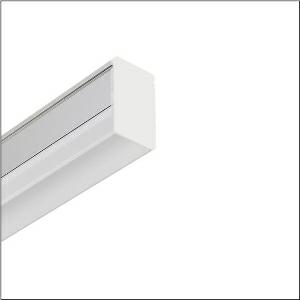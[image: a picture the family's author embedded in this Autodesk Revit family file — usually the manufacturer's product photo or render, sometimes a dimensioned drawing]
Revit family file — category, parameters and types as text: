
# Revit family: siluette_41-f_51lp327km20af
name_source: partatom
category: Lighting Fixtures
units: mm (PartAtom-declared; Revit-internal decimal feet)

## family parameters
Cut with Voids When Loaded = No
Host = Face
Light Source = No
Part Type = Normal
Room Calculation Point = No
Round Connector Dimension = Use Diameter
Shared = No

## types (1)
- --- (1 x LED, 2000 lm, 16 W, 5000K)
    Apparent Load = 16 VA
    CIE Flux Codes = 37 66 87 87 100
    Color Rendering = 80
    Color Temperature = 5000K
    Default Elevation = 1800 mm
    Description = Siluette 41-F, batten luminaire, primary optical cover: cover, of PC, frosted, light emission: direct distribution, primary light characteristic: symmetric, installation type: surface-mounted, LED, rated luminous flux: 2.000lm, luminous efficacy: 125lm/W, light colour: 830/840/850, colour temperature: 3000/4000/5000K, control gear: ON/OFF, with terminal, 2-pole, mains connection: 220..240V, AC, 50/60Hz, rated input power: 16W, housing, of aluminium, silver, length: 1.180mm, width: 25mm, height: 44mm, end cap, of PC, white, protection rating (complete): IP20, insulation class (complete): insulation class II (safety insulation), certification: CE, permissible operating ambient temperature: -20..+40°C, packaging unit: 1 piece
    Height = 44 mm
    Lamp = 1 x LED
    Lamp Light Flux = 2000 lm
    Lamp Power = 16 W
    Lamp count = 1
    Length = 1180 mm
    Luminous efficacy = 125 lm/W
    Manufacturer = Siteco
    ModVariant = No
    Model = 51LP327KM20AF
    Mounting Place = Ceiling
    Mounting Type = Surface mounted
    Number of Poles = 1
    OnlyDefault = Yes
    Power Factor = 1
    Product Name = Siluette 41-F
    Product group = batten luminaire
    ProductGroupID = 303
    Protection Class = Protection class II
    Protection Degree = IP 20
    RLX_Detail_Level = 1
    RLX_Emergency_Light_Flux = 0 lm
    RLX_Emergency_Type = 0
    RLX_Emergency_Type_DB = No
    RlxData = <blob elided: 28417 chars, md5=2e08ef5f>
    Socket = socket
    Standby Power = 0 W
    System Light Flux = 2000 lm
    System Power = 16 W
    Type Comments = individual setting: colour temperature 5000K
    Type Image = l_1007255.jpg
    URL = http://relux.com
    VarID = @adj_037605
    Voltage = 0 V
    Weight = 0.00 kg
    Width = 25 mm  [stored 0.082021 ft]

note: [stored X ft] marks values corroborated as IEEE doubles in the binary element streams (Revit-internal decimal feet)

## geometry (parser evidence)
native form markers: Blend x4, Sweep x11
no freeform markers — native parametric forms only
